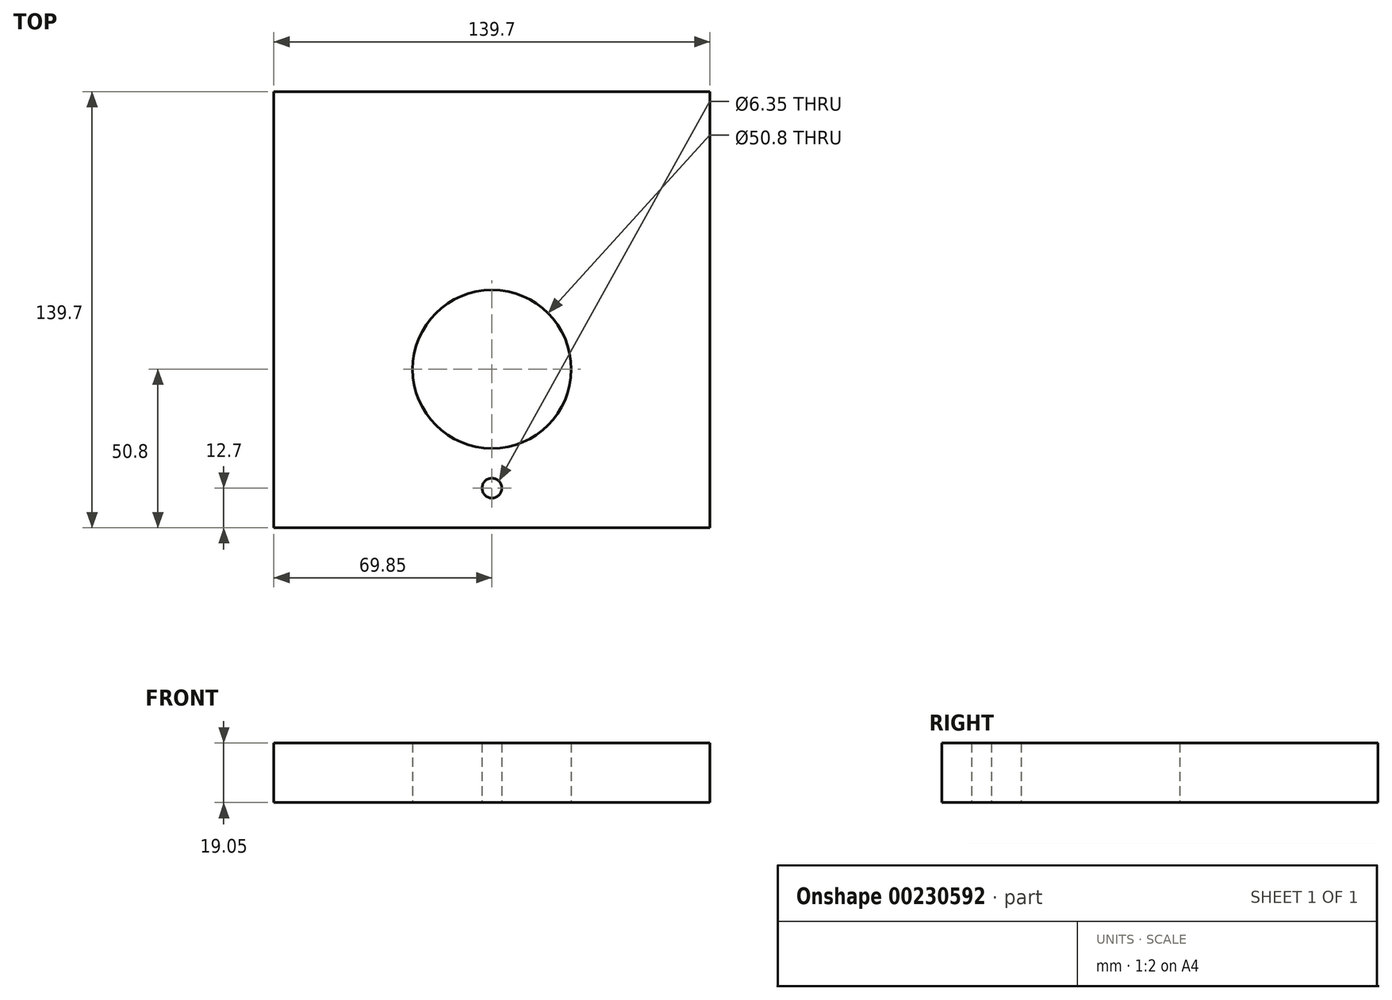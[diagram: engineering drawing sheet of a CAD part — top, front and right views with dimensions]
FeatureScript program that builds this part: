
annotation { "Feature Type Name" : "Feature", "Feature Type Description" : "" }
export const myFeature = defineFeature(function(context is Context, id is Id, definition is map)
    precondition{}
    {
        {
            var Q0;
            Q0=qCreatedBy(makeId("Top.planeOp"),FACE);
            var sketch = newSketch(context, id + "F0", { "sketchPlane" : qUnion([Q0])});
            skLineSegment(sketch, "E0.bottom", {"start": v(69.85, 69.85) * mm, "end": v(-69.85, 69.85) * mm});
            skLineSegment(sketch, "E0.top", {"start": v(69.85, -69.85) * mm, "end": v(-69.85, -69.85) * mm});
            skLineSegment(sketch, "E0.left", {"start": v(69.85, 69.85) * mm, "end": v(69.85, -69.85) * mm});
            skLineSegment(sketch, "E0.right", {"start": v(-69.85, 69.85) * mm, "end": v(-69.85, -69.85) * mm});
            skPoint(sketch, "E0.middle", {"position": v(0, 0) * mm});
            skLineSegment(sketch, "E1", {"start": v(0, -69.85) * mm, "end": v(0, -57.15) * mm});
            skPoint(sketch, "E1.endSnap0", {"position": v(0, -69.85) * mm});
            skLineSegment(sketch, "E2", {"start": v(0, -57.15) * mm, "end": v(0, -19.05) * mm});
            skCircle(sketch, "E3", {"center": v(0, -57.15) * mm, "radius": 3.18 * mm});
            skCircle(sketch, "E4", {"center": v(0, -19.05) * mm, "radius": 25.4 * mm});
            skSolve(sketch);
        }
        {
            var Q0;
            Q0 = qSketchRegion(id + "F0", true);
            extrude(context, id + "F1", {"entities" : qUnion([Q0]), "depth" : 19.05 * mm});
        }
    });
